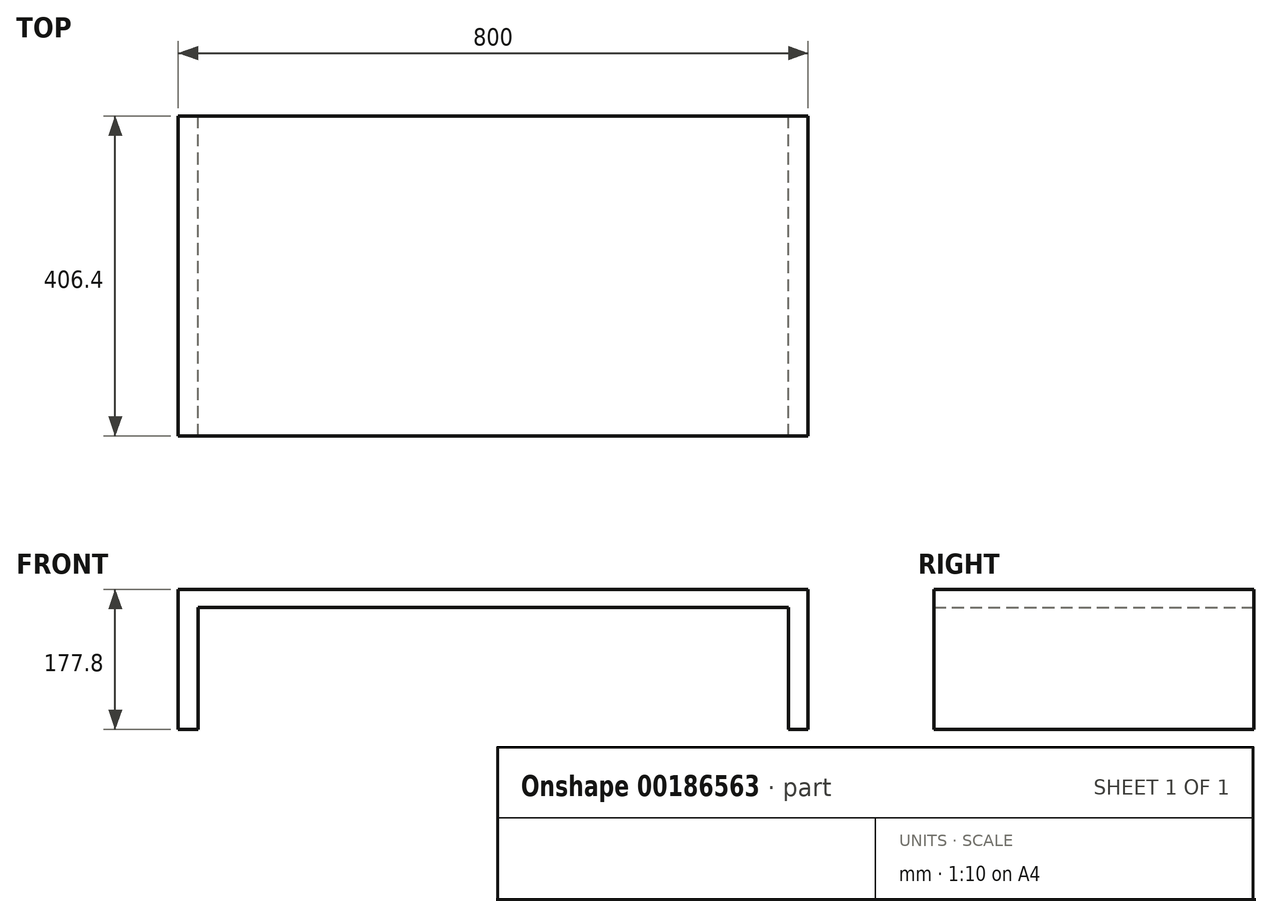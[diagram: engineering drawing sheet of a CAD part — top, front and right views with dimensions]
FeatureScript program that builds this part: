
annotation { "Feature Type Name" : "Feature", "Feature Type Description" : "" }
export const myFeature = defineFeature(function(context is Context, id is Id, definition is map)
    precondition{}
    {
        {
            var Q0;
            Q0=qCreatedBy(makeId("Front.planeOp"),FACE);
            var sketch = newSketch(context, id + "F0", { "sketchPlane" : qUnion([Q0])});
            skLineSegment(sketch, "E0", {"start": v(0, 0) * mm, "end": v(-25, 0) * mm});
            skLineSegment(sketch, "E1", {"start": v(0, 0) * mm, "end": v(0, 154.94) * mm});
            skLineSegment(sketch, "E2", {"start": v(-25, 0) * mm, "end": v(-25, 177.8) * mm});
            skPoint(sketch, "E3.end.orphan", {"position": v(390, 0) * mm});
            skPoint(sketch, "E3.start.orphan", {"position": v(380, 0) * mm});
            skLineSegment(sketch, "E4", {"start": v(0, 154.94) * mm, "end": v(750, 154.94) * mm});
            skLineSegment(sketch, "E5", {"start": v(-25, 177.8) * mm, "end": v(775, 177.8) * mm});
            skLineSegment(sketch, "E6", {"start": v(775, 177.8) * mm, "end": v(775, 0) * mm});
            skLineSegment(sketch, "E7", {"start": v(750, 154.94) * mm, "end": v(750, 0) * mm});
            skLineSegment(sketch, "E8", {"start": v(750, 0) * mm, "end": v(775, 0) * mm});
            skSolve(sketch);
        }
        {
            var Q0;
            Q0 = qSketchRegion(id + "F0", true);
            extrude(context, id + "F1", {"entities" : qUnion([Q0]), "depth" : 406.4 * mm});
        }
    });
